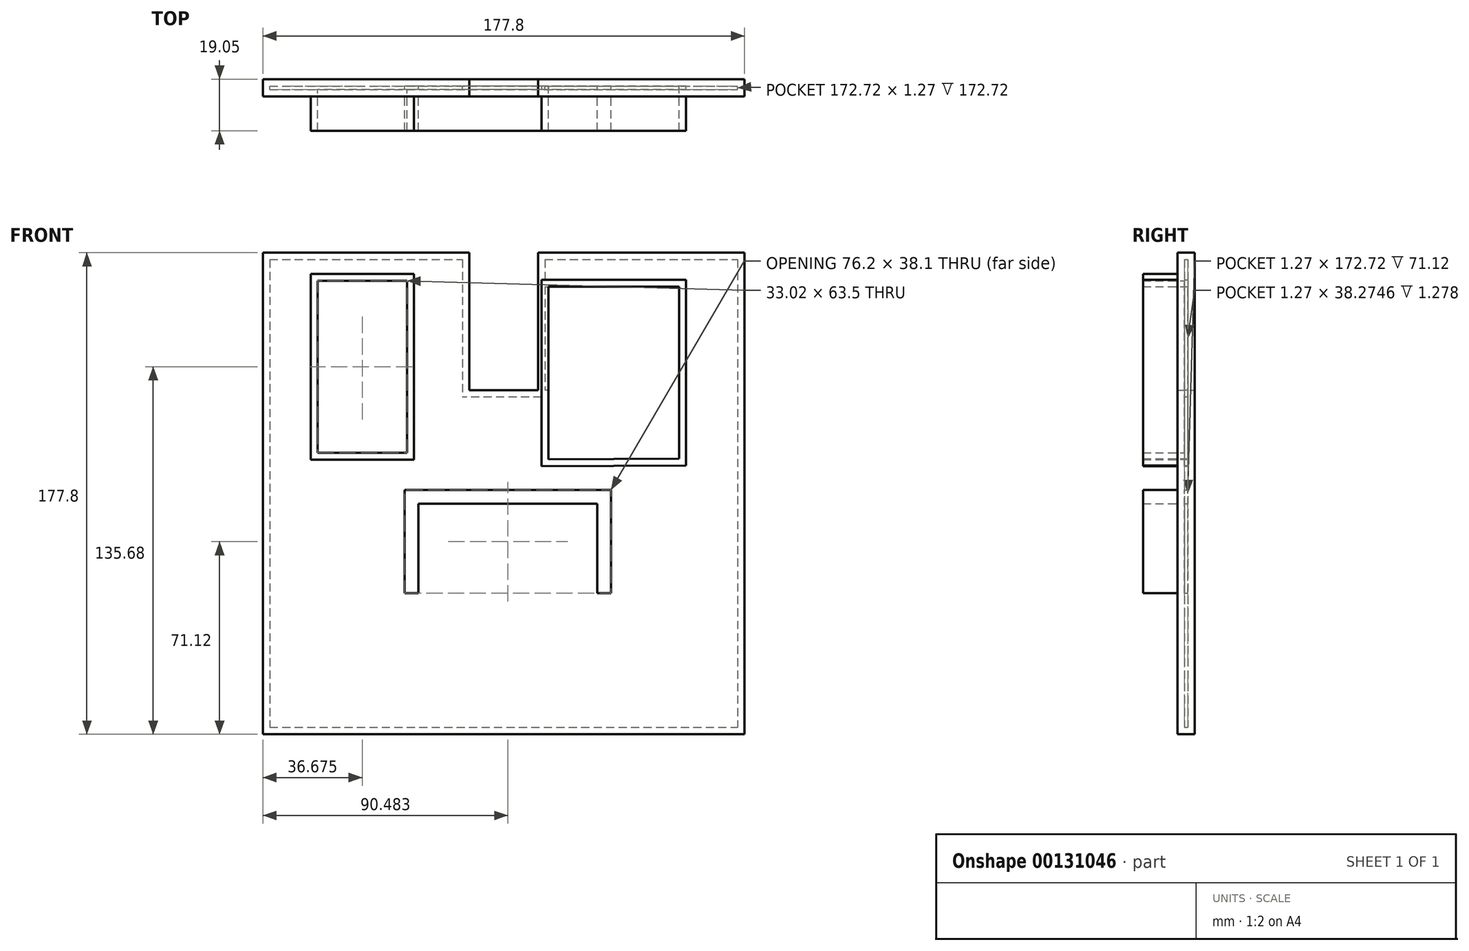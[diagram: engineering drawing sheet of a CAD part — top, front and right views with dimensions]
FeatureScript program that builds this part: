
annotation { "Feature Type Name" : "Feature", "Feature Type Description" : "" }
export const myFeature = defineFeature(function(context is Context, id is Id, definition is map)
    precondition{}
    {
        {
            var Q0;
            Q0=qCreatedBy(makeId("Front.planeOp"),FACE);
            var sketch = newSketch(context, id + "F0", { "sketchPlane" : qUnion([Q0])});
            skLineSegment(sketch, "E0.top", {"start": v(-90.18, -90.17) * mm, "end": v(87.62, -90.17) * mm});
            skLineSegment(sketch, "E0.left", {"start": v(-90.18, 87.63) * mm, "end": v(-90.18, -90.17) * mm});
            skLineSegment(sketch, "E0.right", {"start": v(87.62, 87.63) * mm, "end": v(87.62, -90.17) * mm});
            skLineSegment(sketch, "E1", {"start": v(-13.98, 87.63) * mm, "end": v(-13.98, 36.83) * mm});
            skLineSegment(sketch, "E2", {"start": v(11.42, 87.63) * mm, "end": v(11.42, 36.83) * mm});
            skLineSegment(sketch, "E3", {"start": v(11.42, 36.83) * mm, "end": v(-13.98, 36.83) * mm});
            skPoint(sketch, "E4.start.orphan", {"position": v(-1.28, 87.63) * mm});
            skLineSegment(sketch, "E5", {"start": v(-90.18, 87.63) * mm, "end": v(-13.98, 87.63) * mm});
            skPoint(sketch, "E6.start.orphan", {"position": v(14.94, 87.63) * mm});
            skLineSegment(sketch, "E7", {"start": v(11.42, 87.63) * mm, "end": v(87.62, 87.63) * mm});
            skSolve(sketch);
        }
        {
            var Q0;
            Q0=makeQuery(id+"F0.imprint","IMPRINT",FACE,{"disambiguationData":[TD([[makeQuery(id+"F0.imprint","IMPRINT",EDGE,{"derivedFrom":sQuery(id+"F0.wireOp",EDGE,"E0.top")}),1.0]])]});
            extrude(context, id + "F1", {"entities" : qUnion([Q0]), "depth" : 6.35 * mm});
        }
        {
            var Q0;
            Q0=qCreatedBy(makeId("Front.planeOp"),FACE);
            var sketch = newSketch(context, id + "F2", { "sketchPlane" : qUnion([Q0])});
            skLineSegment(sketch, "E8", {"start": v(-72.56, 79.8) * mm, "end": v(-34.46, 79.8) * mm});
            skLineSegment(sketch, "E9", {"start": v(-72.56, 79.8) * mm, "end": v(-72.56, 11.22) * mm});
            skLineSegment(sketch, "E10", {"start": v(-72.56, 11.22) * mm, "end": v(-34.46, 11.22) * mm});
            skLineSegment(sketch, "E11", {"start": v(-34.46, 11.22) * mm, "end": v(-34.46, 79.8) * mm});
            skSolve(sketch);
        }
        {
            var Q0;
            Q0 = qSketchRegion(id + "F2", true);
            extrude(context, id + "F3", {"entities" : qUnion([Q0]), "operationType" : NewBodyOperationType.ADD, "depth" : 19.05 * mm});
        }
        {
            var Q0;
            Q0=makeQuery(id+"F3.opExtrude","CAP_FACE",FACE,{"disambiguationData":[OSD([sQuery(id+"F2.wireOp",EDGE,"E8"),sQuery(id+"F2.wireOp",EDGE,"E9"),sQuery(id+"F2.wireOp",EDGE,"E10"),sQuery(id+"F2.wireOp",EDGE,"E11")])],"isStart":false});
            shell(context, id + "F4", {"entities" : qUnion([Q0]), "thickness" : 2.54 * mm});
        }
        {
            var Q0;
            Q0=qCreatedBy(makeId("Front.planeOp"),FACE);
            var sketch = newSketch(context, id + "F5", { "sketchPlane" : qUnion([Q0])});
            skLineSegment(sketch, "E12", {"start": v(12.7, 8.79) * mm, "end": v(66.03, 9.07) * mm});
            skLineSegment(sketch, "E13", {"start": v(66.03, 9.07) * mm, "end": v(66.03, 77.65) * mm});
            skLineSegment(sketch, "E14", {"start": v(66.03, 77.65) * mm, "end": v(12.7, 77.65) * mm});
            skLineSegment(sketch, "E15", {"start": v(12.7, 77.65) * mm, "end": v(12.7, 8.79) * mm});
            skSolve(sketch);
        }
        {
            var Q0;
            Q0 = qSketchRegion(id + "F5", true);
            extrude(context, id + "F6", {"entities" : qUnion([Q0]), "operationType" : NewBodyOperationType.ADD, "depth" : 19.05 * mm});
        }
        {
            var Q0;
            Q0=makeQuery(id+"F6.opExtrude","CAP_FACE",FACE,{"disambiguationData":[OSD([sQuery(id+"F5.wireOp",EDGE,"E12"),sQuery(id+"F5.wireOp",EDGE,"E13"),sQuery(id+"F5.wireOp",EDGE,"E14"),sQuery(id+"F5.wireOp",EDGE,"E15")])],"isStart":false});
            shell(context, id + "F7", {"entities" : qUnion([Q0]), "thickness" : 2.54 * mm});
        }
        {
            var Q0;
            Q0=qCreatedBy(makeId("Front.planeOp"),FACE);
            var sketch = newSketch(context, id + "F8", { "sketchPlane" : qUnion([Q0])});
            skLineSegment(sketch, "E16", {"start": v(-37.8, 0) * mm, "end": v(-37.8, -38.1) * mm});
            skLineSegment(sketch, "E17", {"start": v(38.4, 0) * mm, "end": v(38.4, -38.1) * mm});
            skLineSegment(sketch, "E18", {"start": v(-37.8, 0) * mm, "end": v(38.4, 0) * mm});
            skLineSegment(sketch, "E19", {"start": v(-37.8, -38.1) * mm, "end": v(-32.72, -38.1) * mm});
            skLineSegment(sketch, "E20", {"start": v(-32.72, -38.1) * mm, "end": v(-32.72, -5.08) * mm});
            skLineSegment(sketch, "E21", {"start": v(-32.72, -5.08) * mm, "end": v(33.32, -5.08) * mm});
            skLineSegment(sketch, "E22", {"start": v(33.32, -5.08) * mm, "end": v(33.32, -38.1) * mm});
            skLineSegment(sketch, "E23", {"start": v(33.32, -38.1) * mm, "end": v(38.4, -38.1) * mm});
            skSolve(sketch);
        }
        {
            var Q0;
            Q0 = qSketchRegion(id + "F8", true);
            extrude(context, id + "F9", {"entities" : qUnion([Q0]), "operationType" : NewBodyOperationType.ADD, "depth" : 19.05 * mm});
        }
    });
